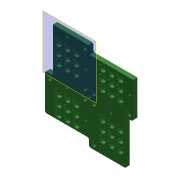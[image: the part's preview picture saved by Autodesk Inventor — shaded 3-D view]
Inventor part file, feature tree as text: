
AUTODESK INVENTOR PART (.ipt)
format: ipt  version: 2019.4 (Build 234330000, 330)  size: 458,752 bytes
history: native  units: mm
features: sketch x5, extrude x4, pattern_linear x3, other x3, projected_geometry x2, plane x1, hole x1, fillet x1, pattern_circular x1, reference x1
ambient origin geometry x8: Origin, YZ Plane, XZ Plane, XY Plane, X Axis, Y Axis, Z Axis, Center Point
bodies: Solid1 (feature_tree)
feature tree (22):
  plane  "Work Plane1"
  extrude  "Extrusion1"  Depth=50.0mm
  pattern_linear  "Rectangular Pattern1"  Count1=5  [1 undecoded]
  hole  "Hole1"  [1 undecoded]
  pattern_linear  "Rectangular Pattern2"  Spacing1=6.0mm  [1 undecoded]
  extrude  "Extrusion4"  Depth=6.0mm
  pattern_linear  "Rectangular Pattern3"  Spacing1=3.0mm  [1 undecoded]
  extrude  "Extrusion5"  Depth=50.0mm
  fillet  "Fillet1"  Radius=50.0mm
  extrude  "Extrusion6"  Depth=9.0mm
  pattern_circular  "Circular Pattern2"  [2 undecoded]
  sketch  "Sketch1"  dims[d0=5.0mm d1=0.0mm d2=20.0mm d4=50.0mm d5=20.0mm d7=50.0mm d10=50.0mm]
  reference  "Reference1"
  sketch  "Sketch3"  dims[d11=50.0mm]
  projected_geometry  "Projected Loop1"
  sketch  "Sketch5"  dims[d12=4.2mm d13=6.0mm d14=8.0mm d15=3.5mm d16=90.0deg d17=8.0mm d18=20.594885mm d19=30.0mm d21=10.0mm d22=30.0mm d24=10.0mm]
  sketch  "Sketch6"  dims[d30=2.9mm]
  projected_geometry  "Projected Loop3"
  sketch  "Sketch7"  dims[d31=2.9mm d32=6.0mm d33=6.0mm d34=3.0mm d35=0.0mm d36=20.0mm d38=50.0mm d39=20.0mm d41=50.0mm d42=9.0mm d43=10.0mm d44=0.0mm d45=2.0mm d46=10.0mm d47=0.0mm d48=40.0mm d49=360.0deg d25=1.0mm d26=1.0mm d27=1.0mm d28=0.15mm d29=0.25mm]
  other  "Application_Fluorescence_Microscope_Infinity_cellstorm_v3.iam"
  other  "10_Base_puzzle_v3:3"
  other  "10_Base_puzzle_v3:16"
note: 6 required parameter values undecoded (feature->parameter linkage not recoverable at this tier; creation-order binding heuristic only, values carry confidence <= 0.55)
